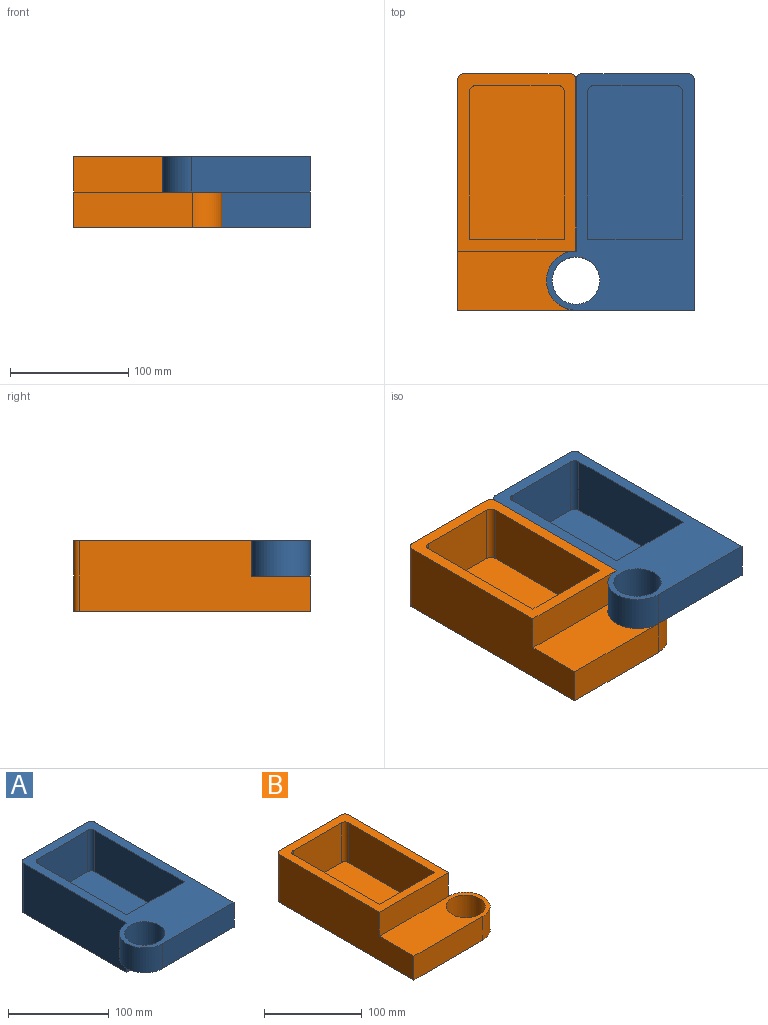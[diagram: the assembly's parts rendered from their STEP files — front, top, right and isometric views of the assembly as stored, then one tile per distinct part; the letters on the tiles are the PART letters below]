
ASSEMBLY  parts=2 mates=1
PART A: 19 faces, bbox 125x200x60 mm
  f0: plane 150x100mm, normal (0,0,-1), area 14989.3mm2, adj f5,f6,f7,f13,f15,f16
  f1: plane 70x50mm, normal (0,-1,0), area 3500mm2, adj f11,f12,f17,f18
  f2: plane 125x50mm, normal (-1,0,0), area 6250mm2, adj f3,f11,f12,f17
  f3: plane 80x50mm, normal (0,1,0), area 4000mm2, adj f2,f10,f11,f12
  f4: plane 100x30mm, normal (0,-1,0), area 3000mm2, adj f5,f8,f11,f14
  f5: plane 195x60mm, normal (1,0,0), area 10200mm2, adj f0,f4,f11,f13,f14,f15
  f6: plane 90x60mm, normal (0,1,0), area 5400mm2, adj f0,f11,f15,f16
  f7: plane 145x60mm, normal (-1,0,0), area 8700mm2, adj f0,f8,f11,f13,f16
  f8: cylinder r=25mm len=50mm, axis (0,0,-1), area 2356.2mm2, adj f4,f7,f11,f14
  f9: cylinder r=20mm len=40mm, axis (0,0,-1), area 3769.9mm2, adj f11,f14
  f10: plane 125x50mm, normal (1,0,0), area 6250mm2, adj f3,f11,f12,f18
  f11: plane 200x125mm, normal (0,0,1), area 9325.1mm2, adj f1,f2,f3,f4,f5,f6,f7,f8
  f12: plane 130x80mm, normal (0,0,1), area 10389.3mm2, adj f1,f2,f3,f10,f17,f18
  f13: plane 100x30mm, normal (0,-1,0), area 3000mm2, adj f0,f5,f7,f14
  f14: plane 125x50mm, normal (0,0,-1), area 4725.1mm2, adj f4,f5,f8,f9,f13
  f15: cylinder r=5mm len=60mm, axis (0,0,1), area 471.2mm2, adj f0,f5,f6,f11
  f16: cylinder r=5mm len=60mm, axis (0,0,-1), area 471.2mm2, adj f0,f6,f7,f11
  f17: cylinder r=5mm len=50mm, axis (0,0,-1), area 392.7mm2, adj f1,f2,f11,f12
  f18: cylinder r=5mm len=50mm, axis (0,0,1), area 392.7mm2, adj f1,f10,f11,f12
PART B: 19 faces, bbox 125x200x60 mm
  f0: plane 125x50mm, normal (1,0,0), area 6250mm2, adj f7,f8,f14,f17
  f1: plane 70x50mm, normal (0,-1,0), area 3500mm2, adj f8,f14,f17,f18
  f2: plane 125x50mm, normal (-1,0,0), area 6250mm2, adj f7,f8,f14,f18
  f3: plane 195x60mm, normal (-1,0,0), area 10200mm2, adj f4,f8,f9,f10,f13,f16
  f4: plane 100x30mm, normal (0,-1,0), area 3000mm2, adj f3,f5,f8,f13
  f5: plane 145x60mm, normal (1,0,0), area 8700mm2, adj f4,f8,f9,f11,f15
  f6: plane 90x60mm, normal (0,1,0), area 5400mm2, adj f8,f9,f15,f16
  f7: plane 80x50mm, normal (0,1,0), area 4000mm2, adj f0,f2,f8,f14
  f8: plane 150x100mm, normal (0,0,1), area 4600mm2, adj f0,f1,f2,f3,f4,f5,f6,f7
  f9: plane 200x125mm, normal (0,0,-1), area 19714.4mm2, adj f3,f5,f6,f10,f11,f12,f15,f16
  f10: plane 100x30mm, normal (0,-1,0), area 3000mm2, adj f3,f9,f11,f13
  f11: cylinder r=25mm len=50mm, axis (0,0,-1), area 2356.2mm2, adj f5,f9,f10,f13
  f12: cylinder r=20mm len=40mm, axis (0,0,-1), area 3769.9mm2, adj f9,f13
  f13: plane 125x50mm, normal (0,0,1), area 4725.1mm2, adj f3,f4,f10,f11,f12
  f14: plane 130x80mm, normal (0,0,1), area 10389.3mm2, adj f0,f1,f2,f7,f17,f18
  f15: cylinder r=5mm len=60mm, axis (0,0,-1), area 471.2mm2, adj f5,f6,f8,f9
  f16: cylinder r=5mm len=60mm, axis (0,0,1), area 471.2mm2, adj f3,f6,f8,f9
  f17: cylinder r=5mm len=50mm, axis (0,0,-1), area 392.7mm2, adj f0,f1,f8,f14
  f18: cylinder r=5mm len=50mm, axis (0,0,1), area 392.7mm2, adj f1,f2,f8,f14
PLACE A t=(125.84,163.31,3.67)mm
PLACE B t=(189.68,95.18,3.67)mm
MATE revolute B.f11 <-> A.f8  axis (0,0,-1) through (89.68,120.18,33.67)mm
